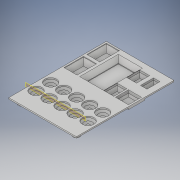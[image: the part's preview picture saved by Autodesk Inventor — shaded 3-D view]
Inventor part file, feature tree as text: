
AUTODESK INVENTOR PART (.ipt)
format: ipt  version: 2018.3 (Build 223284000, 284)  size: 532,480 bytes
history: native  units: in
note: dims shown in document units (in); Inventor stores cm internally (conversion verified against a paired STEP export)
features: sketch x13, extrude x12, chamfer x10, projected_geometry x5, pattern_linear x4, plane x1, revolve x1, fillet x1
ambient origin geometry x8: Origin, YZ Plane, XZ Plane, XY Plane, X Axis, Y Axis, Z Axis, Center Point
bodies: Solid1 (feature_tree)
feature tree (47):
  extrude  "Extrusion1"  Depth=1.0in
  plane  "Work Plane2"
  revolve  "Revolution1"  [1 undecoded]
  fillet  "Fillet1"  Radius=1.0in
  pattern_linear  "Rectangular Pattern1"  Spacing1=0.1in  [1 undecoded]
  pattern_linear  "Rectangular Pattern2"  Spacing1=45.0deg  [1 undecoded]
  extrude  "Extrusion2"  TaperAngle=90.0deg  [1 undecoded]
  extrude  "Extrusion3"  Depth=0.25in
  chamfer  "Chamfer1"  Distance=1.0in
  extrude  "Extrusion4"  Depth=0.3937in
  extrude  "Extrusion5"  Depth=0.125in
  chamfer  "Chamfer2"  Distance=0.125in
  extrude  "Extrusion6"  Depth=0.5in
  extrude  "Extrusion7"  Depth=1.0in
  chamfer  "Chamfer3"  Distance=1.0in
  chamfer  "Chamfer4"  Distance=0.125in
  pattern_linear  "Rectangular Pattern3"  Spacing1=1.2in  [1 undecoded]
  chamfer  "Chamfer5"  Distance=0.6in
  chamfer  "Chamfer6"  Distance=1.0in
  chamfer  "Chamfer7"  Distance=0.125in
  extrude  "Extrusion8"  Depth=0.125in
  extrude  "Extrusion9"  Depth=0.125in
  chamfer  "Chamfer8"  Distance=0.125in
  pattern_linear  "Rectangular Pattern4"  Spacing1=0.3in  [1 undecoded]
  chamfer  "Chamfer9"  Distance=0.05in
  extrude  "Extrusion10"  Depth=0.125in TaperAngle=45.0deg
  extrude  "Extrusion11"  Depth=0.125in
  chamfer  "Chamfer10"  Distance=0.125in
  extrude  "Extrusion12"  Depth=0.125in
  sketch  "Sketch1"  dims[d0=0.9in d1=1.9685in d3=1.0in d4=0.7874in d6=1.125in]
  sketch  "Sketch5"  dims[d9=0.5in d10=0.5in d11=1.0in]
  projected_geometry  "Projected Loop1"
  sketch  "Sketch7"  dims[d12=1.5in]
  sketch  "Sketch8"  dims[d20=1.5in]
  sketch  "Sketch9"  dims[d21=1.25in]
  sketch  "Sketch10"  dims[d22=2.375in]
  sketch  "Sketch11"  dims[d23=1.5in]
  sketch  "Sketch12"  dims[d24=0.6in]
  projected_geometry  "Projected Loop2"
  sketch  "Sketch14"  dims[d26=0.1in d27=0.0in]
  projected_geometry  "Projected Loop3"
  sketch  "Sketch16"  dims[d31=-1.5in]
  projected_geometry  "Projected Loop4"
  sketch  "Sketch18"  dims[d32=0.45in]
  sketch  "Sketch19"  dims[d33=0.2in]
  projected_geometry  "Projected Loop5"
  sketch  "Sketch20"  dims[d34=0.1in d35=0.1in d36=45.0deg d37=90.0deg d38=0.25in d39=1.5748in d41=1.0in d42=0.7874in d44=1.125in d45=0.7874in d47=1.75in d48=0.3937in d50=1.0in d52=0.125in d53=0.125in d54=0.5in d55=1.0in d56=1.0in d57=0.125in d58=1.2in d59=0.6in d60=0.7874in d62=1.0in d63=0.125in d64=0.125in d65=0.125in d66=0.125in d67=0.3in d68=0.0in d69=0.05in d70=0.0in d71=0.125in d72=0.125in d73=45.0deg d74=0.125in d75=0.125in d76=0.125in d77=0.125in d78=0.3in d79=0.0in d80=0.05in d81=0.0in d82=0.3in d83=0.125in d84=45.0deg d85=0.3in d86=0.125in d87=0.125in d88=0.125in d89=0.125in d90=0.3in d91=0.0in d92=0.05in d93=0.0in d94=0.3in d95=0.125in d96=45.0deg d97=0.2in d98=0.125in d99=45.0deg d100=0.7874in d102=1.75in d103=0.3in d104=0.125in d105=45.0deg d106=0.2in d107=0.125in d108=45.0deg d109=0.2in d110=0.125in d111=45.0deg d114=0.75in d115=1.0in d116=0.125in d117=0.125in d118=0.125in d119=0.125in d120=0.125in d121=0.3in d122=0.0in d123=0.05in d124=0.0in d125=0.2in d126=0.125in d127=45.0deg d128=0.7874in d130=1.75in d131=0.3937in d133=1.0in d135=0.7874in d137=1.75in d138=0.2in d139=0.125in d140=45.0deg d141=0.5in d142=1.0in d143=0.125in d144=0.125in d145=0.125in d146=0.125in d147=0.3in d148=0.0in d149=0.05in d150=0.0in d151=0.2in d152=0.125in d153=45.0deg d154=0.5in d155=0.5in d156=0.5in d157=0.5in d158=0.5in d159=0.5in d160=0.3in d161=0.0in]
note: 6 required parameter values undecoded (feature->parameter linkage not recoverable at this tier; creation-order binding heuristic only, values carry confidence <= 0.55)